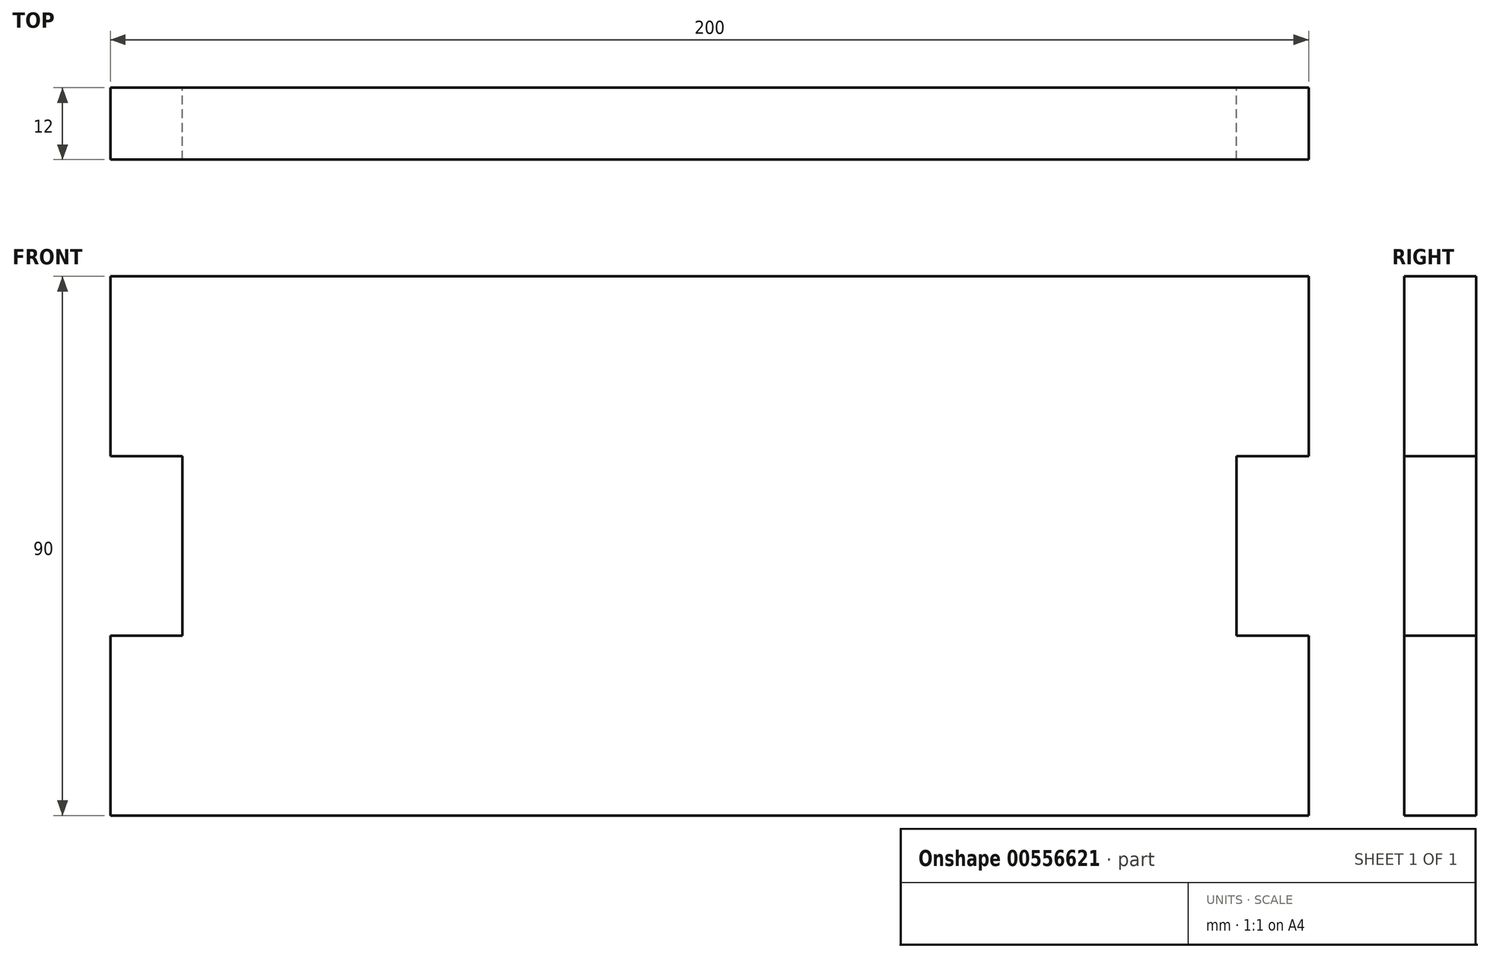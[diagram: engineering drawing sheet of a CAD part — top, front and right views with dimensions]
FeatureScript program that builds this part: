
annotation { "Feature Type Name" : "Feature", "Feature Type Description" : "" }
export const myFeature = defineFeature(function(context is Context, id is Id, definition is map)
    precondition{}
    {
        {
            var Q0;
            Q0=qCreatedBy(makeId("Front.planeOp"),FACE);
            var sketch = newSketch(context, id + "F0", { "sketchPlane" : qUnion([Q0])});
            skLineSegment(sketch, "E0", {"start": v(0, 0) * mm, "end": v(0, 30) * mm});
            skLineSegment(sketch, "E1", {"start": v(0, 30) * mm, "end": v(12, 30) * mm});
            skLineSegment(sketch, "E2", {"start": v(12, 30) * mm, "end": v(12, 60) * mm});
            skLineSegment(sketch, "E3", {"start": v(12, 60) * mm, "end": v(0, 60) * mm});
            skLineSegment(sketch, "E4", {"start": v(0, 60) * mm, "end": v(0, 90) * mm});
            skLineSegment(sketch, "E5", {"start": v(0, 90) * mm, "end": v(100, 90) * mm});
            skLineSegment(sketch, "E6", {"start": v(100, 90) * mm, "end": v(100, 0) * mm, "construction": true});
            skLineSegment(sketch, "E7", {"start": v(100, 0) * mm, "end": v(0, 0) * mm});
            skLineSegment(sketch, "E8.MirrorCS", {"start": v(188, 60) * mm, "end": v(200, 60) * mm});
            skLineSegment(sketch, "E9.MirrorCS", {"start": v(100, 0) * mm, "end": v(200, 0) * mm});
            skLineSegment(sketch, "E10.MirrorCS", {"start": v(200, 60) * mm, "end": v(200, 90) * mm});
            skLineSegment(sketch, "E11.MirrorCS", {"start": v(188, 30) * mm, "end": v(188, 60) * mm});
            skLineSegment(sketch, "E12.MirrorCS", {"start": v(200, 0) * mm, "end": v(200, 30) * mm});
            skLineSegment(sketch, "E13.MirrorCS", {"start": v(200, 90) * mm, "end": v(100, 90) * mm});
            skLineSegment(sketch, "E14.MirrorCS", {"start": v(200, 30) * mm, "end": v(188, 30) * mm});
            skSolve(sketch);
        }
        {
            var Q0;
            Q0=makeQuery(id+"F0.imprint","IMPRINT",FACE,{"disambiguationData":[TD([[makeQuery(id+"F0.imprint","IMPRINT",EDGE,{"derivedFrom":sQuery(id+"F0.wireOp",EDGE,"E0")}),-1.0]])]});
            extrude(context, id + "F1", {"entities" : qUnion([Q0]), "endBound" : BoundingType.SYMMETRIC, "depth" : 12 * mm, "offsetDistance" : 25 * mm});
        }
    });
